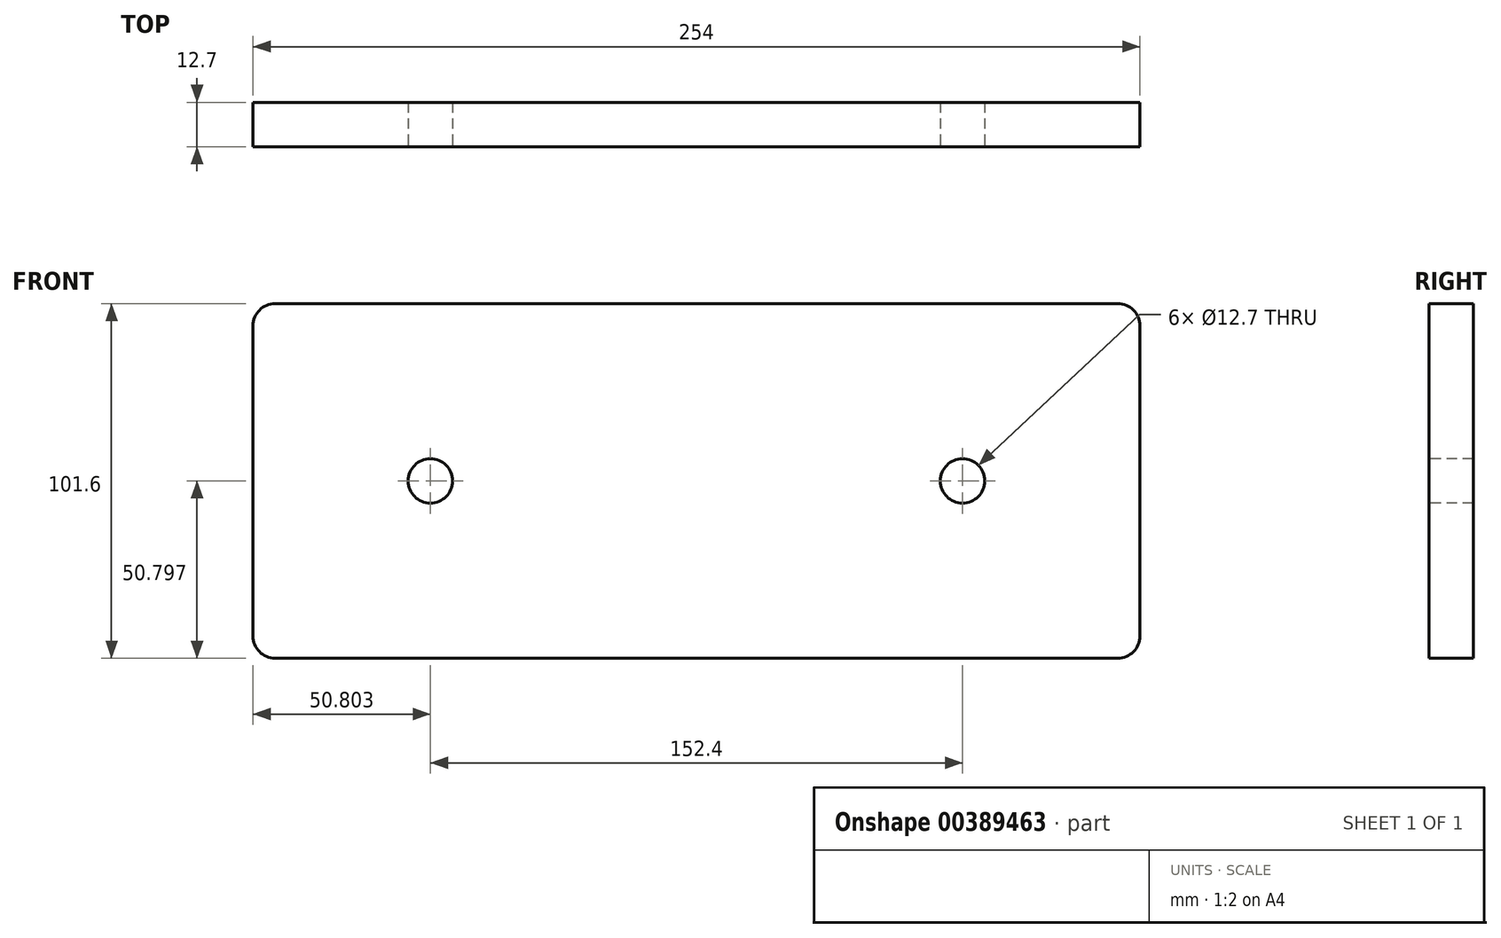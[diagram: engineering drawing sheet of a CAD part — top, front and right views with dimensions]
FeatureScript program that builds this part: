
annotation { "Feature Type Name" : "Feature", "Feature Type Description" : "" }
export const myFeature = defineFeature(function(context is Context, id is Id, definition is map)
    precondition{}
    {
        {
            var Q0;
            Q0=qCreatedBy(makeId("Front.planeOp"),FACE);
            var sketch = newSketch(context, id + "F0", { "sketchPlane" : qUnion([Q0])});
            skLineSegment(sketch, "E0.bottom", {"start": v(-200.5, 85.12) * mm, "end": v(53.5, 85.12) * mm});
            skLineSegment(sketch, "E0.top", {"start": v(-200.5, -16.48) * mm, "end": v(53.5, -16.48) * mm});
            skLineSegment(sketch, "E0.left", {"start": v(-200.5, 85.12) * mm, "end": v(-200.5, -16.48) * mm});
            skLineSegment(sketch, "E0.right", {"start": v(53.5, 85.12) * mm, "end": v(53.5, -16.48) * mm});
            skSolve(sketch);
        }
        {
            var Q0;
            Q0 = qSketchRegion(id + "F0", true);
            extrude(context, id + "F1", {"entities" : qUnion([Q0]), "depth" : 12.7 * mm});
        }
        {
            var Q0;
            Q0=makeQuery(id+"F1.opExtrude","SWEPT_EDGE",EDGE,{"disambiguationData":[OSD([sQuery(id+"F0.wireOp",EDGE,"E0.bottom"),sQuery(id+"F0.wireOp",EDGE,"E0.left")])]});
            var Q1;
            Q1=makeQuery(id+"F1.opExtrude","SWEPT_EDGE",EDGE,{"disambiguationData":[OSD([sQuery(id+"F0.wireOp",EDGE,"E0.top"),sQuery(id+"F0.wireOp",EDGE,"E0.left")])]});
            var Q2;
            Q2=makeQuery(id+"F1.opExtrude","SWEPT_EDGE",EDGE,{"disambiguationData":[OSD([sQuery(id+"F0.wireOp",EDGE,"E0.top"),sQuery(id+"F0.wireOp",EDGE,"E0.right")])]});
            var Q3;
            Q3=makeQuery(id+"F1.opExtrude","SWEPT_EDGE",EDGE,{"disambiguationData":[OSD([sQuery(id+"F0.wireOp",EDGE,"E0.bottom"),sQuery(id+"F0.wireOp",EDGE,"E0.right")])]});
            fillet(context, id + "F2", {"entities" : qUnion([Q0, Q1, Q2, Q3]), "radius" : 6.35 * mm, "tangentPropagation" : true, "allowEdgeOverflow" : false});
        }
        {
            var Q0;
            Q0=makeQuery(id+"F1.opExtrude","CAP_FACE",FACE,{"disambiguationData":[OSD([sQuery(id+"F0.wireOp",EDGE,"E0.bottom"),sQuery(id+"F0.wireOp",EDGE,"E0.top"),sQuery(id+"F0.wireOp",EDGE,"E0.left"),sQuery(id+"F0.wireOp",EDGE,"E0.right")])],"isStart":false});
            var sketch = newSketch(context, id + "F3", { "sketchPlane" : qUnion([Q0])});
            skPoint(sketch, "E1", {"position": v(-149.7, 34.32) * mm});
            skPoint(sketch, "E2", {"position": v(2.7, 34.32) * mm});
            skSolve(sketch);
        }
        {
            var Q0;
            Q0=sQuery(id+"F3.wireOp",VERTEX,"E1");
            var Q1;
            Q1=sQuery(id+"F3.wireOp",VERTEX,"E2");
            var Q2;
            Q2=makeQuery(id+"F1.opExtrude","SWEPT_BODY",BODY,{"disambiguationData":[OSD([sQuery(id+"F0.wireOp",EDGE,"E0.bottom"),sQuery(id+"F0.wireOp",EDGE,"E0.top"),sQuery(id+"F0.wireOp",EDGE,"E0.left"),sQuery(id+"F0.wireOp",EDGE,"E0.right")])]});
            hole(context, id + "F4", {"style" : HoleStyle.SIMPLE, "endStyle" : HoleEndStyle.THROUGH, "holeDiameter" : 12.7 * mm, "isTappedThrough" : true, "tappedDepth" : 12.7 * mm, "tapClearance" : 3, "locations" : qUnion([Q0, Q1]), "scope" : qUnion([Q2])});
        }
    });
